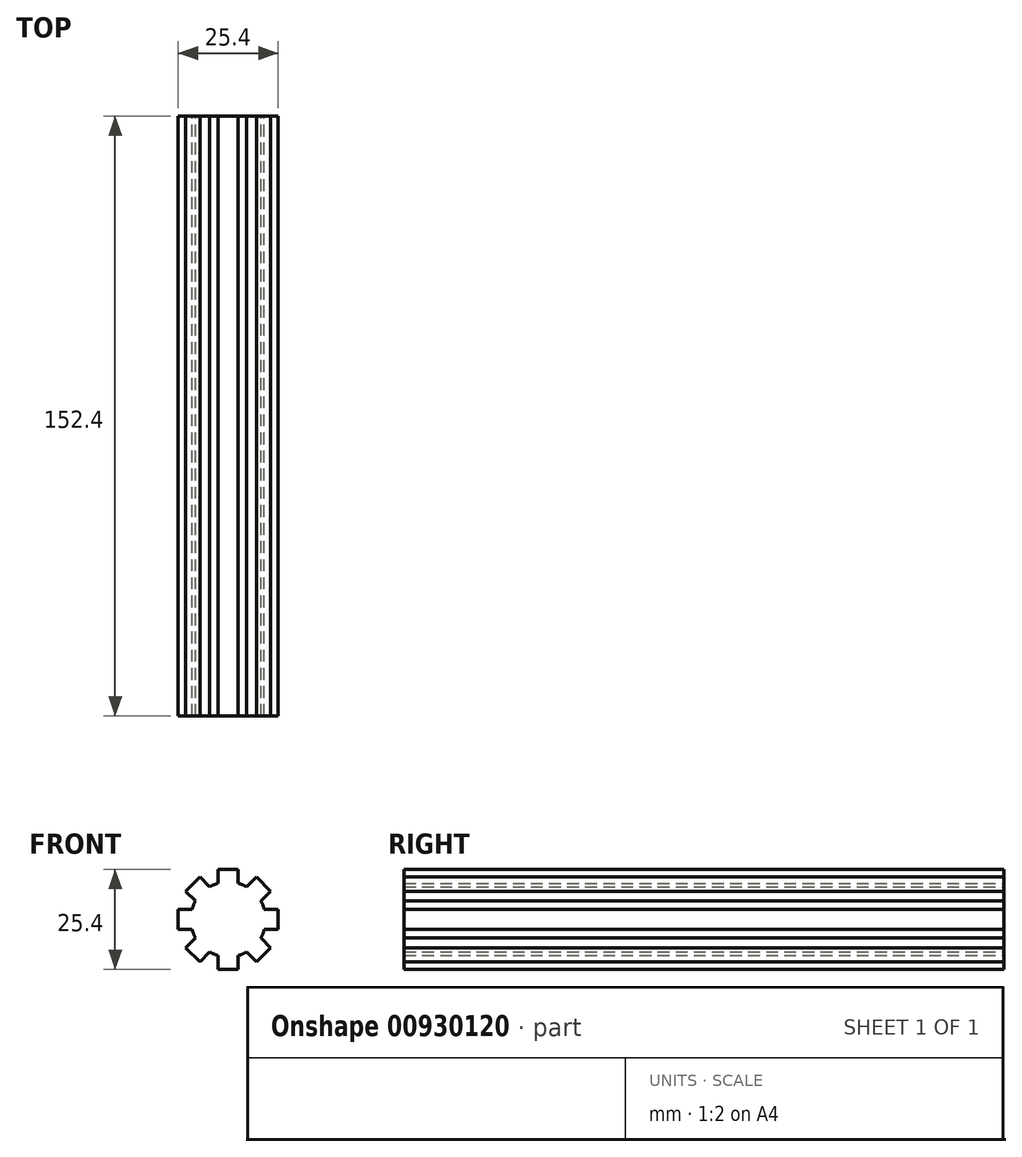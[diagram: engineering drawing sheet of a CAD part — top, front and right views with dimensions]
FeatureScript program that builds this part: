
annotation { "Feature Type Name" : "Feature", "Feature Type Description" : "" }
export const myFeature = defineFeature(function(context is Context, id is Id, definition is map)
    precondition{}
    {
        {
            var Q0;
            Q0=qCreatedBy(makeId("Front.planeOp"),FACE);
            var sketch = newSketch(context, id + "F0", { "sketchPlane" : qUnion([Q0])});
            skLineSegment(sketch, "E0.bottom", {"start": v(-2.54, 12.7) * mm, "end": v(2.54, 12.7) * mm});
            skLineSegment(sketch, "E0.top", {"start": v(-2.54, -12.7) * mm, "end": v(2.54, -12.7) * mm});
            skLineSegment(sketch, "E0.left", {"start": v(-2.54, 12.7) * mm, "end": v(-2.54, 9.18) * mm});
            skLineSegment(sketch, "E0.right", {"start": v(2.54, 12.7) * mm, "end": v(2.54, 9.18) * mm});
            skPoint(sketch, "E0.middle", {"position": v(0, 0) * mm});
            skLineSegment(sketch, "E1.bottom", {"start": v(-12.7, 2.54) * mm, "end": v(-9.18, 2.54) * mm});
            skLineSegment(sketch, "E1.top", {"start": v(-12.7, -2.54) * mm, "end": v(-9.18, -2.54) * mm});
            skLineSegment(sketch, "E1.left", {"start": v(-12.7, 2.54) * mm, "end": v(-12.7, -2.54) * mm});
            skLineSegment(sketch, "E1.right", {"start": v(12.7, 2.54) * mm, "end": v(12.7, -2.54) * mm});
            skLineSegment(sketch, "E2", {"start": v(8.98, 8.98) * mm, "end": v(7.18, 10.78) * mm});
            skLineSegment(sketch, "E3.MirrorCS", {"start": v(8.98, 8.98) * mm, "end": v(10.78, 7.18) * mm});
            skLineSegment(sketch, "E4.MirrorCS", {"start": v(-8.98, -8.98) * mm, "end": v(-7.18, -10.78) * mm});
            skLineSegment(sketch, "E5.MirrorCS", {"start": v(-8.98, -8.98) * mm, "end": v(-10.78, -7.18) * mm});
            skLineSegment(sketch, "E6", {"start": v(7.18, 10.78) * mm, "end": v(4.7, 8.29) * mm});
            skLineSegment(sketch, "E7", {"start": v(-7.18, -10.78) * mm, "end": v(-4.7, -8.29) * mm});
            skLineSegment(sketch, "E8", {"start": v(8.98, -8.98) * mm, "end": v(7.18, -10.78) * mm});
            skLineSegment(sketch, "E9.MirrorCS", {"start": v(-8.98, 8.98) * mm, "end": v(-10.78, 7.18) * mm});
            skLineSegment(sketch, "E10.MirrorCS", {"start": v(8.98, -8.98) * mm, "end": v(10.78, -7.18) * mm});
            skLineSegment(sketch, "E11.MirrorCS", {"start": v(-8.98, 8.98) * mm, "end": v(-7.18, 10.78) * mm});
            skLineSegment(sketch, "E12", {"start": v(-7.18, 10.78) * mm, "end": v(-4.7, 8.29) * mm});
            skLineSegment(sketch, "E13", {"start": v(7.18, -10.78) * mm, "end": v(4.7, -8.29) * mm});
            skArc(sketch, "E14", {"start": v(-8.29, 4.7) * mm, "mid": v(-8.8, 3.65) * mm, "end": v(-9.18, 2.54) * mm});
            skLineSegment(sketch, "E15.trimOffspring", {"start": v(-8.29, -4.7) * mm, "end": v(-10.78, -7.18) * mm});
            skLineSegment(sketch, "E16.trimOffspring", {"start": v(-8.29, 4.7) * mm, "end": v(-10.78, 7.18) * mm});
            skPoint(sketch, "E17.orphan", {"position": v(-8.98, 8.98) * mm});
            skArc(sketch, "E18.trimOffspring", {"start": v(-2.54, 9.18) * mm, "mid": v(-3.65, 8.8) * mm, "end": v(-4.7, 8.29) * mm});
            skLineSegment(sketch, "E19.trimOffspring", {"start": v(-2.54, -9.18) * mm, "end": v(-2.54, -12.7) * mm});
            skArc(sketch, "E20.trimOffspring", {"start": v(2.54, -9.18) * mm, "mid": v(3.65, -8.8) * mm, "end": v(4.7, -8.29) * mm});
            skArc(sketch, "E21.trimOffspring", {"start": v(-4.7, -8.29) * mm, "mid": v(-3.65, -8.8) * mm, "end": v(-2.54, -9.18) * mm});
            skArc(sketch, "E22.trimOffspring", {"start": v(-9.18, -2.54) * mm, "mid": v(-8.8, -3.65) * mm, "end": v(-8.29, -4.7) * mm});
            skArc(sketch, "E23.trimOffspring", {"start": v(4.7, 8.29) * mm, "mid": v(3.65, 8.8) * mm, "end": v(2.54, 9.18) * mm});
            skArc(sketch, "E24.trimOffspring", {"start": v(9.18, 2.54) * mm, "mid": v(8.8, 3.65) * mm, "end": v(8.29, 4.7) * mm});
            skLineSegment(sketch, "E25.trimOffspring", {"start": v(8.29, 4.7) * mm, "end": v(10.78, 7.18) * mm});
            skLineSegment(sketch, "E26.trimOffspring", {"start": v(2.54, -9.18) * mm, "end": v(2.54, -12.7) * mm});
            skArc(sketch, "E27.trimOffspring", {"start": v(8.29, -4.7) * mm, "mid": v(8.8, -3.65) * mm, "end": v(9.18, -2.54) * mm});
            skLineSegment(sketch, "E28.trimOffspring", {"start": v(8.29, -4.7) * mm, "end": v(10.78, -7.18) * mm});
            skLineSegment(sketch, "E29.trimOffspring", {"start": v(9.18, -2.54) * mm, "end": v(12.7, -2.54) * mm});
            skLineSegment(sketch, "E30.trimOffspring", {"start": v(9.18, 2.54) * mm, "end": v(12.7, 2.54) * mm});
            skSolve(sketch);
        }
        {
            var Q0;
            Q0=makeQuery(id+"F0.imprint","IMPRINT",FACE,{"disambiguationData":[TD([[makeQuery(id+"F0.imprint","IMPRINT",EDGE,{"derivedFrom":sQuery(id+"F0.wireOp",EDGE,"E0.bottom")}),-1.0]])]});
            extrude(context, id + "F1", {"entities" : qUnion([Q0]), "depth" : 152.4 * mm, "offsetDistance" : 25.4 * mm});
        }
    });
